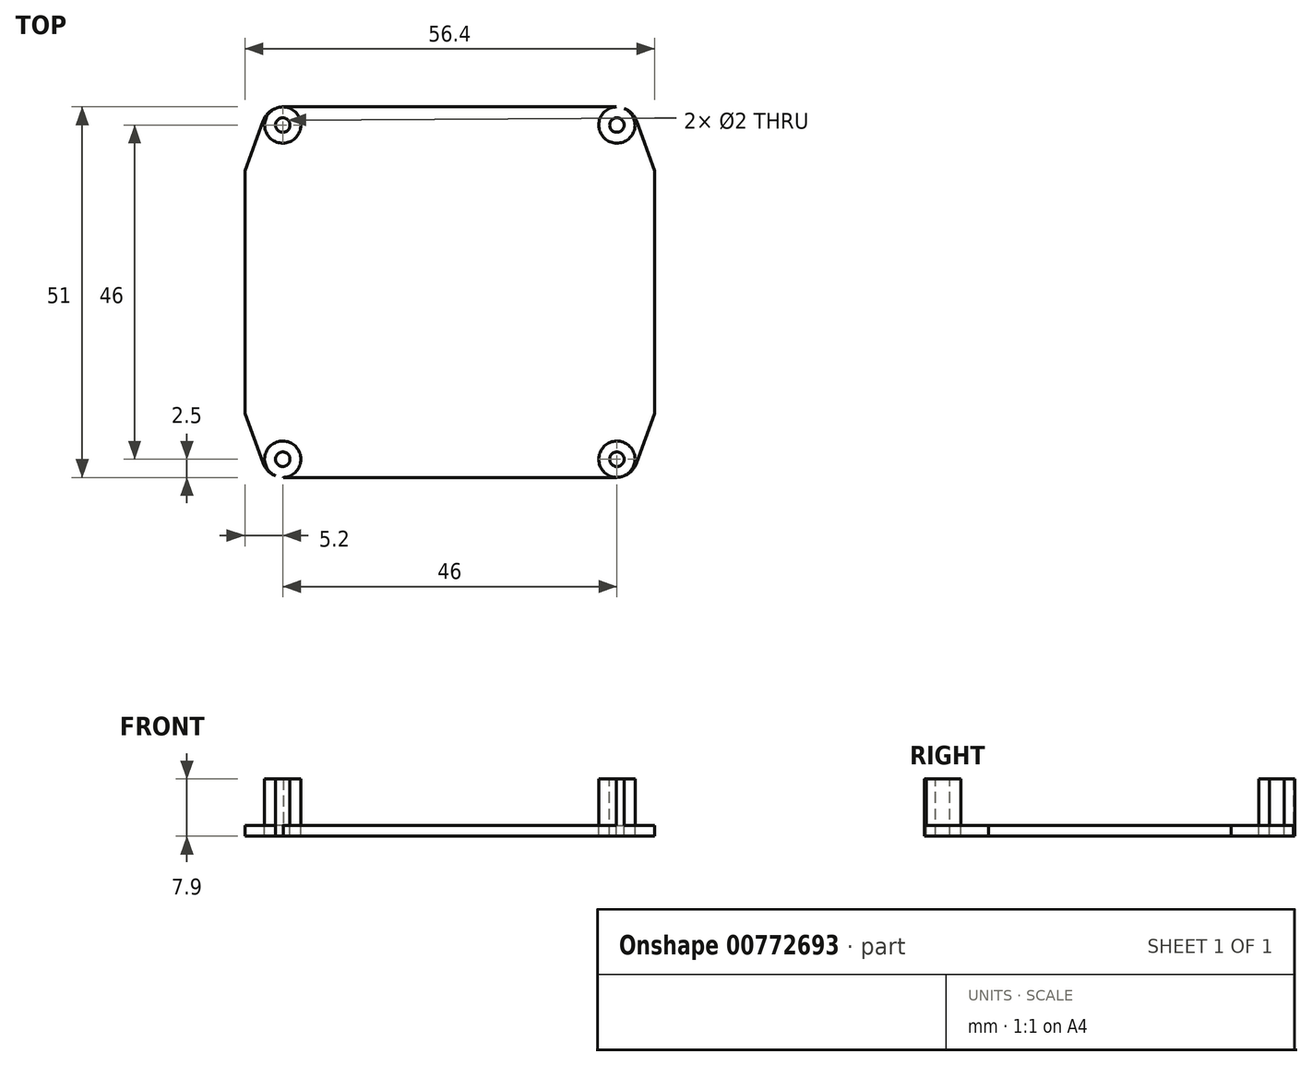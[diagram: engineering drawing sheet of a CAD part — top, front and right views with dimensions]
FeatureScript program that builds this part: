
annotation { "Feature Type Name" : "Feature", "Feature Type Description" : "" }
export const myFeature = defineFeature(function(context is Context, id is Id, definition is map)
    precondition{}
    {
        {
            var Q0;
            Q0=qCreatedBy(makeId("Top.planeOp"),FACE);
            var sketch = newSketch(context, id + "F0", { "sketchPlane" : qUnion([Q0])});
            skLineSegment(sketch, "E0", {"start": v(-28.2, 16.7) * mm, "end": v(-25.72, 23.53) * mm});
            skLineSegment(sketch, "E1", {"start": v(-22.9, 25.5) * mm, "end": v(22.9, 25.5) * mm});
            skLineSegment(sketch, "E2", {"start": v(25.72, 23.53) * mm, "end": v(28.2, 16.7) * mm});
            skLineSegment(sketch, "E3", {"start": v(-28.2, -16.7) * mm, "end": v(-25.72, -23.53) * mm});
            skLineSegment(sketch, "E4", {"start": v(-22.9, -25.5) * mm, "end": v(22.9, -25.5) * mm});
            skLineSegment(sketch, "E5", {"start": v(25.72, -23.53) * mm, "end": v(28.2, -16.7) * mm});
            skPoint(sketch, "E6.visualSharp", {"position": v(-25, -25.5) * mm});
            skArc(sketch, "E6.filletArc", {"start": v(-25.72, -23.53) * mm, "mid": v(-24.62, -24.96) * mm, "end": v(-22.9, -25.5) * mm});
            skPoint(sketch, "E7.visualSharp", {"position": v(25, -25.5) * mm});
            skArc(sketch, "E7.filletArc", {"start": v(22.9, -25.5) * mm, "mid": v(24.62, -24.96) * mm, "end": v(25.72, -23.53) * mm});
            skPoint(sketch, "E8.visualSharp", {"position": v(25, 25.5) * mm});
            skArc(sketch, "E8.filletArc", {"start": v(25.72, 23.53) * mm, "mid": v(24.62, 24.96) * mm, "end": v(22.9, 25.5) * mm});
            skPoint(sketch, "E9.visualSharp", {"position": v(-25, 25.5) * mm});
            skArc(sketch, "E9.filletArc", {"start": v(-22.9, 25.5) * mm, "mid": v(-24.62, 24.96) * mm, "end": v(-25.72, 23.53) * mm});
            skCircle(sketch, "E10", {"center": v(-23, 23) * mm, "radius": 2.5 * mm});
            skCircle(sketch, "E11.MirrorC", {"center": v(23, 23) * mm, "radius": 2.5 * mm});
            skCircle(sketch, "E12", {"center": v(-23, 23) * mm, "radius": 1 * mm});
            skCircle(sketch, "E13.MirrorC", {"center": v(23, 23) * mm, "radius": 1 * mm});
            skLineSegment(sketch, "E14", {"start": v(-28.2, 16.7) * mm, "end": v(-28.2, -16.7) * mm});
            skLineSegment(sketch, "E15", {"start": v(28.2, 16.7) * mm, "end": v(28.2, -16.7) * mm});
            skCircle(sketch, "E16.MirrorC", {"center": v(23, -23) * mm, "radius": 2.5 * mm});
            skCircle(sketch, "E17.MirrorC", {"center": v(23, -23) * mm, "radius": 1 * mm});
            skCircle(sketch, "E18.MirrorC", {"center": v(-23, -23) * mm, "radius": 1 * mm});
            skCircle(sketch, "E19.MirrorC", {"center": v(-23, -23) * mm, "radius": 2.5 * mm});
            skSolve(sketch);
        }
        {
            var Q0;
            {var subQ11=sQuery(id+"F0.wireOp",EDGE,"E0");Q0=makeQuery(id+"F0.imprint","IMPRINT",FACE,{"disambiguationData":[TD([[makeQuery(id+"F0.imprint","IMPRINT",EDGE,{"derivedFrom":subQ11}),-1.0]])]});}
            var Q1;
            Q1=makeQuery(id+"F0.imprint","IMPRINT",FACE,{"disambiguationData":[TD([[makeQuery(id+"F0.imprint","IMPRINT",EDGE,{"derivedFrom":sQuery(id+"F0.wireOp",EDGE,"E12")}),-1.0]])]});
            var Q2;
            Q2=makeQuery(id+"F0.imprint","IMPRINT",FACE,{"disambiguationData":[TD([[makeQuery(id+"F0.imprint","IMPRINT",EDGE,{"derivedFrom":sQuery(id+"F0.wireOp",EDGE,"E13.MirrorC")}),1.0]])]});
            var Q3;
            Q3=makeQuery(id+"F0.imprint","IMPRINT",FACE,{"disambiguationData":[TD([[makeQuery(id+"F0.imprint","IMPRINT",EDGE,{"derivedFrom":sQuery(id+"F0.wireOp",EDGE,"E17.MirrorC")}),-1.0]])]});
            var Q4;
            Q4=makeQuery(id+"F0.imprint","IMPRINT",FACE,{"disambiguationData":[TD([[makeQuery(id+"F0.imprint","IMPRINT",EDGE,{"derivedFrom":sQuery(id+"F0.wireOp",EDGE,"E18.MirrorC")}),1.0]])]});
            extrude(context, id + "F1", {"entities" : qUnion([Q0, Q1, Q2, Q3, Q4]), "oppositeDirection" : true, "depth" : 1.5 * mm, "offsetDistance" : 25 * mm});
        }
        {
            var Q0;
            Q0=makeQuery(id+"F0.imprint","IMPRINT",FACE,{"disambiguationData":[TD([[makeQuery(id+"F0.imprint","IMPRINT",EDGE,{"derivedFrom":sQuery(id+"F0.wireOp",EDGE,"E13.MirrorC")}),1.0]])]});
            var Q1;
            Q1=makeQuery(id+"F0.imprint","IMPRINT",FACE,{"disambiguationData":[TD([[makeQuery(id+"F0.imprint","IMPRINT",EDGE,{"derivedFrom":sQuery(id+"F0.wireOp",EDGE,"E12")}),-1.0]])]});
            var Q2;
            Q2=makeQuery(id+"F0.imprint","IMPRINT",FACE,{"disambiguationData":[TD([[makeQuery(id+"F0.imprint","IMPRINT",EDGE,{"derivedFrom":sQuery(id+"F0.wireOp",EDGE,"E18.MirrorC")}),1.0]])]});
            var Q3;
            Q3=makeQuery(id+"F0.imprint","IMPRINT",FACE,{"disambiguationData":[TD([[makeQuery(id+"F0.imprint","IMPRINT",EDGE,{"derivedFrom":sQuery(id+"F0.wireOp",EDGE,"E17.MirrorC")}),-1.0]])]});
            extrude(context, id + "F2", {"entities" : qUnion([Q0, Q1, Q2, Q3]), "operationType" : NewBodyOperationType.ADD, "depth" : 6.4 * mm, "offsetDistance" : 25 * mm});
        }
    });
